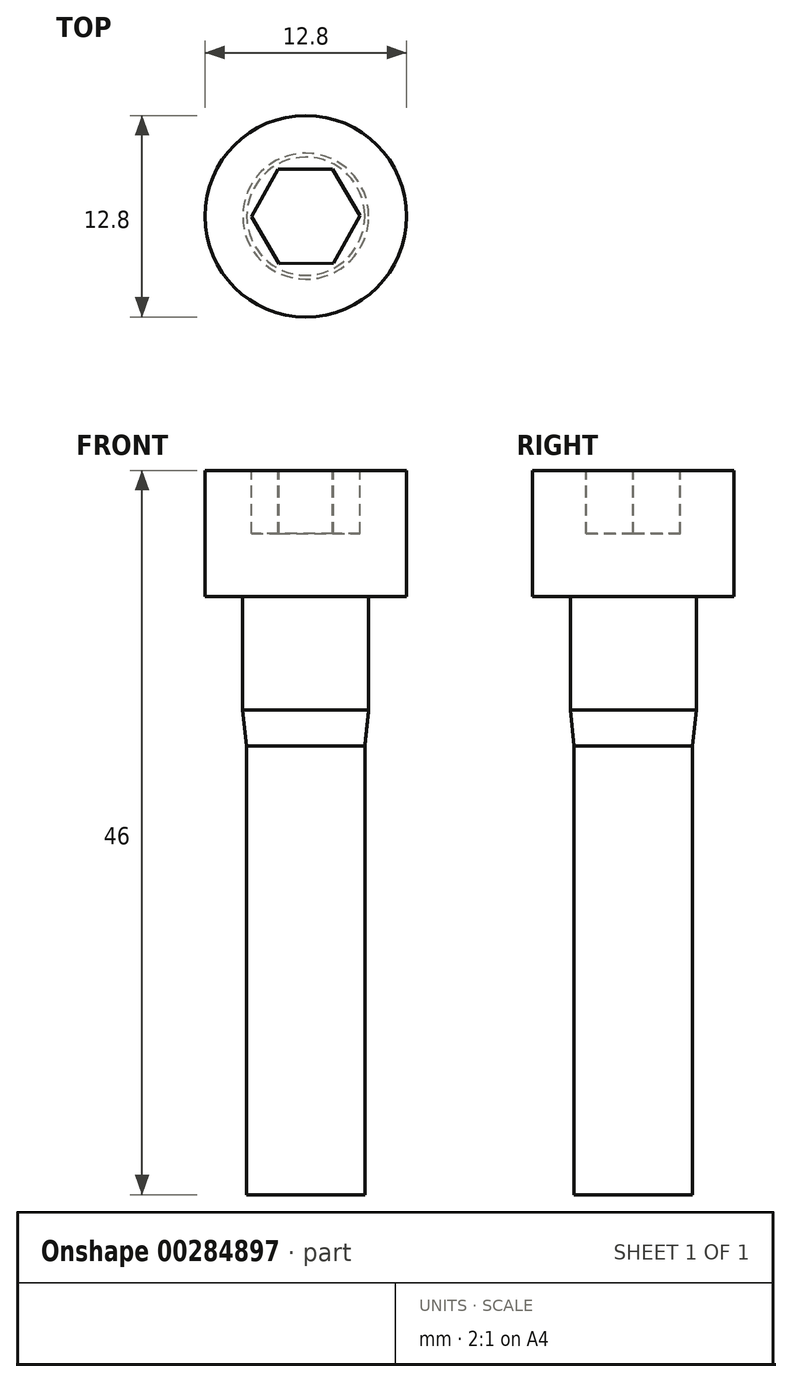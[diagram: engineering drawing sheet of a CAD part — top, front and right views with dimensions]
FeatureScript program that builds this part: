
annotation { "Feature Type Name" : "Feature", "Feature Type Description" : "" }
export const myFeature = defineFeature(function(context is Context, id is Id, definition is map)
    precondition{}
    {
        {
            var Q0;
            Q0=qCreatedBy(makeId("Front.planeOp"),FACE);
            var sketch = newSketch(context, id + "F0", { "sketchPlane" : qUnion([Q0])});
            skLineSegment(sketch, "E0", {"start": v(-3.75, -4.04) * mm, "end": v(0, -4.04) * mm});
            skLineSegment(sketch, "E1", {"start": v(-3.75, -4.04) * mm, "end": v(-3.75, 24.46) * mm});
            skLineSegment(sketch, "E2", {"start": v(-3.75, 24.46) * mm, "end": v(-4, 26.76) * mm});
            skLineSegment(sketch, "E3", {"start": v(-4, 26.76) * mm, "end": v(-4, 33.96) * mm});
            skLineSegment(sketch, "E4", {"start": v(-4, 33.96) * mm, "end": v(-6.4, 33.96) * mm});
            skLineSegment(sketch, "E5", {"start": v(-6.4, 33.96) * mm, "end": v(-6.4, 41.96) * mm});
            skLineSegment(sketch, "E6", {"start": v(-6.4, 41.96) * mm, "end": v(0, 41.96) * mm});
            skLineSegment(sketch, "E7", {"start": v(0, 41.96) * mm, "end": v(0, -4.04) * mm});
            skSolve(sketch);
        }
        {
            var Q0;
            Q0=makeQuery(id+"F0.imprint","IMPRINT",FACE,{"disambiguationData":[TD([[makeQuery(id+"F0.imprint","IMPRINT",EDGE,{"derivedFrom":sQuery(id+"F0.wireOp",EDGE,"E0")}),1.0]])]});
            var Q1;
            Q1=sQuery(id+"F0.wireOp",EDGE,"E7");
            revolve(context, id + "F1", {"surfaceOperationType" : NewSurfaceOperationType.NEW, "entities" : qUnion([Q0]), "axis" : qUnion([Q1]), "revolveType" : RevolveType.FULL});
        }
        {
            var Q0;
            Q0=makeQuery(id+"F1.opRevolve","SWEPT_FACE",FACE,{"disambiguationData":[OSD([sQuery(id+"F0.wireOp",EDGE,"E6")])]});
            var sketch = newSketch(context, id + "F2", { "sketchPlane" : qUnion([Q0])});
            skCircle(sketch, "E8.cCircle", {"center": v(0, 0) * mm, "radius": 2.99 * mm, "construction": true});
            skLineSegment(sketch, "E8.0", {"start": v(-3.45, -0.03) * mm, "end": v(-1.75, 2.97) * mm});
            skLineSegment(sketch, "E8.1", {"start": v(-1.75, 2.97) * mm, "end": v(1.7, 3) * mm});
            skLineSegment(sketch, "E8.2", {"start": v(1.7, 3) * mm, "end": v(3.45, 0.03) * mm});
            skLineSegment(sketch, "E8.3", {"start": v(3.45, 0.03) * mm, "end": v(1.75, -2.97) * mm});
            skLineSegment(sketch, "E8.4", {"start": v(1.75, -2.97) * mm, "end": v(-1.7, -3) * mm});
            skLineSegment(sketch, "E8.5", {"start": v(-1.7, -3) * mm, "end": v(-3.45, -0.03) * mm});
            skPoint(sketch, "E8.0.midPoint", {"position": v(-2.6, 1.47) * mm});
            skSolve(sketch);
        }
        {
            var Q0;
            Q0=makeQuery(id+"F2.imprint","IMPRINT",FACE,{"disambiguationData":[TD([[makeQuery(id+"F2.imprint","IMPRINT",EDGE,{"derivedFrom":sQuery(id+"F2.wireOp",EDGE,"E8.0")}),-1.0]])]});
            extrude(context, id + "F3", {"entities" : qUnion([Q0]), "operationType" : NewBodyOperationType.REMOVE, "oppositeDirection" : true, "depth" : 4 * mm, "offsetDistance" : 25.4 * mm});
        }
    });
